# Revit family: Winkel 40-5 3-Loch L und K
name_source: partatom
category: HLS-Bauteile
revit_build: Autodesk Revit 2017 (Build: 20190507_1515(x64)
units: mm (PartAtom-declared; Revit-internal decimal feet)

## family parameters
Arbeitsebenenbasiert = Ja
Beim Laden mit Abzugskörper schneiden = Nein
Bemaßung runder Anschluss = Durchmesser verwenden
Gemeinsam genutzt = Ja
Immer vertikal = Nein
Raumberechnungspunkt = Nein
Teiletyp = Normal

## types (2) — shared parameters
Anzahl Befestigungsloch = 3 St
B = 40 mm  [stored 0.131234 ft]
Breite Material = 40 mm
Fabrikat = MEFA
Firma = MEFA Befestigungs- und Montagesysteme GmbH
L1 = 103 mm
Lochdurchmesser = 13 mm
Länge Schenkel 1 = 103 mm
Material = Stahl
Mengeneinheit = St
Oberflaeche = galvanisch verzinkt
Profil = C-Profil
Profiltyp = 45
S = 5 mm  [stored 0.0164042 ft]
Stärke Material = 5 mm  [stored 0.0164042 ft]
Vorgabe-Ansicht = 1219 mm
Winkel = 90 °
zero-valued in all types: Sicherheitsfaktor, max. Rohraußendurchmesser, min. Rohraußendurchmesser

## per-type parameters (varying)
| type | Artikelnummer | EAN | Gewicht | Gewicht pro Bauteil | Kurztext1 | Kurztext2 | L2 | Länge Schenkel 2 | vpe |
| Winkel 40-5 3-Loch L | 08140300 | 4250928419750 | 0.23 kg | 0.23 kg | Winkel 3-Loch L C-Profil 45 | 90 ° Schenkel 102.5 x 65 mm | 65 mm  [stored 0.213255 ft] | 65 mm  [stored 0.213255 ft] | 25 St |
| Winkel 40-5 3-Loch K | 08140400 | 4250928419767 | 0.20 kg | 0.20 kg | Winkel 3-Loch K C-Profil 45 | 90 ° Schenkel 102.5 x 45 mm | 45 mm  [stored 0.147638 ft] | 45 mm  [stored 0.147638 ft] | 50 St |

note: [stored X ft] marks values corroborated as IEEE doubles in the binary element streams (Revit-internal decimal feet)
